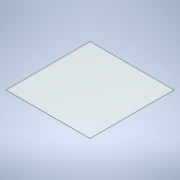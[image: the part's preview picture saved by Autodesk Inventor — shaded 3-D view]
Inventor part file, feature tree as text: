
AUTODESK INVENTOR PART (.ipt)
format: ipt  version: 2022 (Build 260153000, 153)  size: 93,184 bytes
history: native  units: mm
features: other x1, extrude x1, sketch x1
ambient origin geometry x8: Origin, YZ Plane, XZ Plane, XY Plane, X Axis, Y Axis, Z Axis, Center Point
bodies: Body1 (feature_tree)
feature tree (3):
  other  "Sólido1"
  extrude  "Extrusão1"  Depth=430.0mm
  sketch  "Esboço1"  dims[d0=430.0mm d1=430.0mm d2=3.0mm d3=0.0mm]
